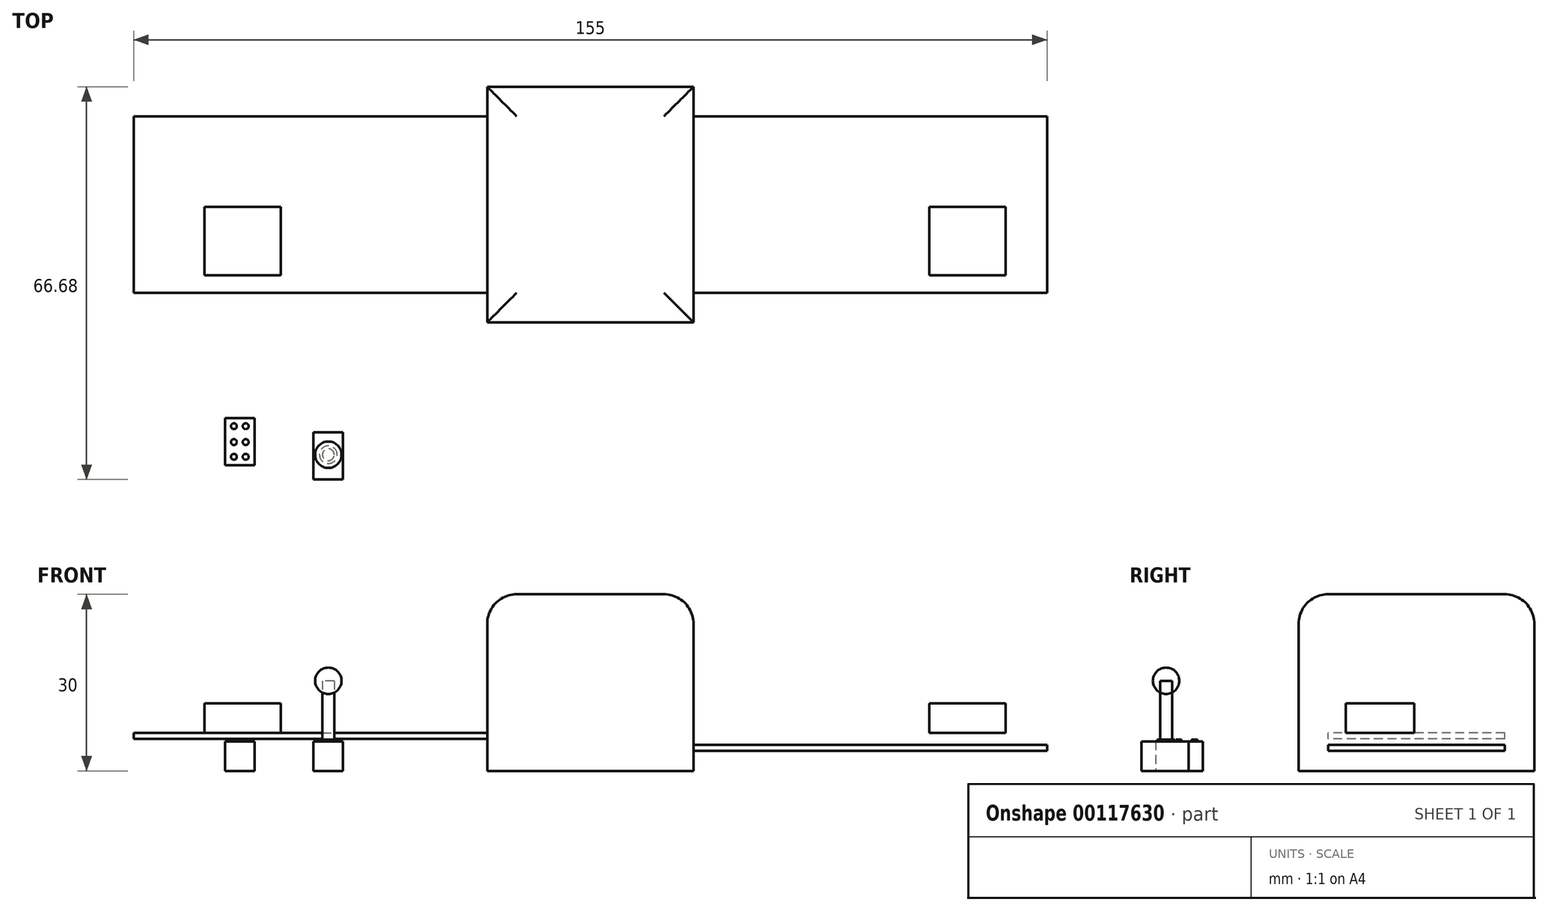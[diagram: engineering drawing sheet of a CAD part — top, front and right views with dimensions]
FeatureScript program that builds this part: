
annotation { "Feature Type Name" : "Feature", "Feature Type Description" : "" }
export const myFeature = defineFeature(function(context is Context, id is Id, definition is map)
    precondition{}
    {
        {
            var Q0;
            Q0=qCreatedBy(makeId("Top.planeOp"),FACE);
            var sketch = newSketch(context, id + "F0", { "sketchPlane" : qUnion([Q0])});
            skLineSegment(sketch, "E0.bottom", {"start": v(-16.65, 20.38) * mm, "end": v(18.35, 20.38) * mm});
            skLineSegment(sketch, "E0.top", {"start": v(-16.65, -19.62) * mm, "end": v(18.35, -19.62) * mm});
            skLineSegment(sketch, "E0.left", {"start": v(-16.65, 20.38) * mm, "end": v(-16.65, -19.62) * mm});
            skLineSegment(sketch, "E0.right", {"start": v(18.35, 20.38) * mm, "end": v(18.35, -19.62) * mm});
            skSolve(sketch);
        }
        {
            var Q0;
            Q0=makeQuery(id+"F0.imprint","IMPRINT",FACE,{"disambiguationData":[TD([[makeQuery(id+"F0.imprint","IMPRINT",EDGE,{"derivedFrom":sQuery(id+"F0.wireOp",EDGE,"E0.bottom")}),-1.0]])]});
            extrude(context, id + "F1", {"entities" : qUnion([Q0]), "depth" : 30 * mm});
        }
        {
            var Q0;
            Q0=makeQuery(id+"F1.opExtrude","CAP_EDGE",EDGE,{"disambiguationData":[OSD([sQuery(id+"F0.wireOp",EDGE,"E0.left")])],"isStart":false});
            var Q1;
            Q1=makeQuery(id+"F1.opExtrude","CAP_EDGE",EDGE,{"disambiguationData":[OSD([sQuery(id+"F0.wireOp",EDGE,"E0.right")])],"isStart":false});
            var Q2;
            Q2=makeQuery(id+"F1.opExtrude","CAP_EDGE",EDGE,{"disambiguationData":[OSD([sQuery(id+"F0.wireOp",EDGE,"E0.bottom")])],"isStart":false});
            var Q3;
            Q3=makeQuery(id+"F1.opExtrude","CAP_EDGE",EDGE,{"disambiguationData":[OSD([sQuery(id+"F0.wireOp",EDGE,"E0.top")])],"isStart":false});
            fillet(context, id + "F2", {"entities" : qUnion([Q0, Q1, Q2, Q3]), "radius" : 5 * mm, "tangentPropagation" : true, "allowEdgeOverflow" : false});
        }
        {
            var Q0;
            Q0=makeQuery(id+"F1.opExtrude","SWEPT_FACE",FACE,{"disambiguationData":[OSD([sQuery(id+"F0.wireOp",EDGE,"E0.right")])]});
            var sketch = newSketch(context, id + "F3", { "sketchPlane" : qUnion([Q0])});
            skLineSegment(sketch, "E1.bottom", {"start": v(15.38, 4.43) * mm, "end": v(-14.62, 4.43) * mm});
            skLineSegment(sketch, "E1.top", {"start": v(15.38, 3.43) * mm, "end": v(-14.62, 3.43) * mm});
            skLineSegment(sketch, "E1.left", {"start": v(15.38, 4.43) * mm, "end": v(15.38, 3.43) * mm});
            skLineSegment(sketch, "E1.right", {"start": v(-14.62, 4.43) * mm, "end": v(-14.62, 3.43) * mm});
            skSolve(sketch);
        }
        {
            var Q0;
            Q0=makeQuery(id+"F3.imprint","IMPRINT",FACE,{"disambiguationData":[TD([[makeQuery(id+"F3.imprint","IMPRINT",EDGE,{"derivedFrom":sQuery(id+"F3.wireOp",EDGE,"E1.bottom")}),1.0]])]});
            extrude(context, id + "F4", {"entities" : qUnion([Q0]), "operationType" : NewBodyOperationType.ADD, "depth" : 60 * mm});
        }
        {
            var Q0;
            Q0=makeQuery(id+"F1.opExtrude","SWEPT_FACE",FACE,{"disambiguationData":[OSD([sQuery(id+"F0.wireOp",EDGE,"E0.left")])]});
            var sketch = newSketch(context, id + "F5", { "sketchPlane" : qUnion([Q0])});
            skLineSegment(sketch, "E2.bottom", {"start": v(-15.38, 5.45) * mm, "end": v(14.62, 5.45) * mm});
            skLineSegment(sketch, "E2.top", {"start": v(-15.38, 6.45) * mm, "end": v(14.62, 6.45) * mm});
            skLineSegment(sketch, "E2.left", {"start": v(-15.38, 5.45) * mm, "end": v(-15.38, 6.45) * mm});
            skLineSegment(sketch, "E2.right", {"start": v(14.62, 5.45) * mm, "end": v(14.62, 6.45) * mm});
            skSolve(sketch);
        }
        {
            var Q0;
            Q0=makeQuery(id+"F5.imprint","IMPRINT",FACE,{"disambiguationData":[TD([[makeQuery(id+"F5.imprint","IMPRINT",EDGE,{"derivedFrom":sQuery(id+"F5.wireOp",EDGE,"E2.bottom")}),1.0]])]});
            extrude(context, id + "F6", {"entities" : qUnion([Q0]), "operationType" : NewBodyOperationType.ADD, "depth" : 60 * mm});
        }
        {
            var Q0;
            Q0=makeQuery(id+"F6.opExtrude","SWEPT_FACE",FACE,{"disambiguationData":[OSD([sQuery(id+"F5.wireOp",EDGE,"E2.top")])]});
            var sketch = newSketch(context, id + "F7", { "sketchPlane" : qUnion([Q0])});
            skLineSegment(sketch, "E3.bottom", {"start": v(-64.65, 0) * mm, "end": v(-51.65, 0) * mm});
            skLineSegment(sketch, "E3.top", {"start": v(-64.65, -11.62) * mm, "end": v(-51.65, -11.62) * mm});
            skLineSegment(sketch, "E3.left", {"start": v(-64.65, 0) * mm, "end": v(-64.65, -11.62) * mm});
            skLineSegment(sketch, "E3.right", {"start": v(-51.65, 0) * mm, "end": v(-51.65, -11.62) * mm});
            skLineSegment(sketch, "E4.bottom", {"start": v(58.35, 0) * mm, "end": v(71.35, 0) * mm});
            skLineSegment(sketch, "E4.top", {"start": v(58.35, -11.62) * mm, "end": v(71.35, -11.62) * mm});
            skLineSegment(sketch, "E4.left", {"start": v(58.35, 0) * mm, "end": v(58.35, -11.62) * mm});
            skLineSegment(sketch, "E4.right", {"start": v(71.35, 0) * mm, "end": v(71.35, -11.62) * mm});
            skSolve(sketch);
        }
        {
            var Q0;
            Q0=makeQuery(id+"F7.imprint","IMPRINT",FACE,{"disambiguationData":[TD([[makeQuery(id+"F7.imprint","IMPRINT",EDGE,{"derivedFrom":sQuery(id+"F7.wireOp",EDGE,"E3.bottom")}),-1.0]])]});
            var Q1;
            Q1=makeQuery(id+"F7.imprint","IMPRINT",FACE,{"disambiguationData":[TD([[makeQuery(id+"F7.imprint","IMPRINT",EDGE,{"derivedFrom":sQuery(id+"F7.wireOp",EDGE,"E4.bottom")}),-1.0]])]});
            extrude(context, id + "F8", {"entities" : qUnion([Q0, Q1]), "operationType" : NewBodyOperationType.ADD, "depth" : 5 * mm});
        }
        {
            var Q0;
            Q0=qCreatedBy(makeId("Top.planeOp"),FACE);
            var sketch = newSketch(context, id + "F9", { "sketchPlane" : qUnion([Q0])});
            skLineSegment(sketch, "E5.bottom", {"start": v(-61.14, -35.86) * mm, "end": v(-56.14, -35.86) * mm});
            skLineSegment(sketch, "E5.top", {"start": v(-61.14, -43.86) * mm, "end": v(-56.14, -43.86) * mm});
            skLineSegment(sketch, "E5.left", {"start": v(-61.14, -35.86) * mm, "end": v(-61.14, -43.86) * mm});
            skLineSegment(sketch, "E5.right", {"start": v(-56.14, -35.86) * mm, "end": v(-56.14, -43.86) * mm});
            skLineSegment(sketch, "E6.bottom", {"start": v(-46.14, -38.3) * mm, "end": v(-41.14, -38.3) * mm});
            skLineSegment(sketch, "E6.top", {"start": v(-46.14, -46.3) * mm, "end": v(-41.14, -46.3) * mm});
            skLineSegment(sketch, "E6.left", {"start": v(-46.14, -38.3) * mm, "end": v(-46.14, -46.3) * mm});
            skLineSegment(sketch, "E6.right", {"start": v(-41.14, -38.3) * mm, "end": v(-41.14, -46.3) * mm});
            skSolve(sketch);
        }
        {
            var Q0;
            Q0=makeQuery(id+"F9.imprint","IMPRINT",FACE,{"disambiguationData":[TD([[makeQuery(id+"F9.imprint","IMPRINT",EDGE,{"derivedFrom":sQuery(id+"F9.wireOp",EDGE,"E5.bottom")}),-1.0]])]});
            var Q1;
            Q1=makeQuery(id+"F9.imprint","IMPRINT",FACE,{"disambiguationData":[TD([[makeQuery(id+"F9.imprint","IMPRINT",EDGE,{"derivedFrom":sQuery(id+"F9.wireOp",EDGE,"E6.bottom")}),-1.0]])]});
            extrude(context, id + "F10", {"entities" : qUnion([Q0, Q1]), "depth" : 5 * mm});
        }
        {
            var Q0;
            Q0=makeQuery(id+"F10.opExtrude","CAP_FACE",FACE,{"disambiguationData":[OSD([sQuery(id+"F9.wireOp",EDGE,"E5.bottom"),sQuery(id+"F9.wireOp",EDGE,"E5.top"),sQuery(id+"F9.wireOp",EDGE,"E5.left"),sQuery(id+"F9.wireOp",EDGE,"E5.right")])],"isStart":false});
            var sketch = newSketch(context, id + "F11", { "sketchPlane" : qUnion([Q0])});
            skCircle(sketch, "E7", {"center": v(-59.64, -37.26) * mm, "radius": 0.5 * mm});
            skCircle(sketch, "E8", {"center": v(-57.64, -37.26) * mm, "radius": 0.5 * mm});
            skCircle(sketch, "E9", {"center": v(-59.64, -39.96) * mm, "radius": 0.5 * mm});
            skCircle(sketch, "E10", {"center": v(-57.64, -39.96) * mm, "radius": 0.5 * mm});
            skCircle(sketch, "E11", {"center": v(-59.64, -42.46) * mm, "radius": 0.5 * mm});
            skCircle(sketch, "E12", {"center": v(-57.64, -42.46) * mm, "radius": 0.5 * mm});
            skSolve(sketch);
        }
        {
            var Q0;
            Q0=makeQuery(id+"F11.imprint","IMPRINT",FACE,{"disambiguationData":[TD([[makeQuery(id+"F11.imprint","IMPRINT",EDGE,{"derivedFrom":sQuery(id+"F11.wireOp",EDGE,"E7")}),1.0]])]});
            var Q1;
            Q1=makeQuery(id+"F11.imprint","IMPRINT",FACE,{"disambiguationData":[TD([[makeQuery(id+"F11.imprint","IMPRINT",EDGE,{"derivedFrom":sQuery(id+"F11.wireOp",EDGE,"E8")}),1.0]])]});
            var Q2;
            Q2=makeQuery(id+"F11.imprint","IMPRINT",FACE,{"disambiguationData":[TD([[makeQuery(id+"F11.imprint","IMPRINT",EDGE,{"derivedFrom":sQuery(id+"F11.wireOp",EDGE,"E9")}),1.0]])]});
            var Q3;
            Q3=makeQuery(id+"F11.imprint","IMPRINT",FACE,{"disambiguationData":[TD([[makeQuery(id+"F11.imprint","IMPRINT",EDGE,{"derivedFrom":sQuery(id+"F11.wireOp",EDGE,"E10")}),1.0]])]});
            var Q4;
            Q4=makeQuery(id+"F11.imprint","IMPRINT",FACE,{"disambiguationData":[TD([[makeQuery(id+"F11.imprint","IMPRINT",EDGE,{"derivedFrom":sQuery(id+"F11.wireOp",EDGE,"E11")}),1.0]])]});
            var Q5;
            Q5=makeQuery(id+"F11.imprint","IMPRINT",FACE,{"disambiguationData":[TD([[makeQuery(id+"F11.imprint","IMPRINT",EDGE,{"derivedFrom":sQuery(id+"F11.wireOp",EDGE,"E12")}),1.0]])]});
            extrude(context, id + "F12", {"entities" : qUnion([Q0, Q1, Q2, Q3, Q4, Q5]), "operationType" : NewBodyOperationType.ADD, "depth" : 0.3 * mm});
        }
        {
            var Q0;
            Q0=makeQuery(id+"F10.opExtrude","CAP_FACE",FACE,{"disambiguationData":[OSD([sQuery(id+"F9.wireOp",EDGE,"E6.bottom"),sQuery(id+"F9.wireOp",EDGE,"E6.top"),sQuery(id+"F9.wireOp",EDGE,"E6.left"),sQuery(id+"F9.wireOp",EDGE,"E6.right")])],"isStart":false});
            var sketch = newSketch(context, id + "F13", { "sketchPlane" : qUnion([Q0])});
            skCircle(sketch, "E13", {"center": v(-43.61, -42.1) * mm, "radius": 1.5 * mm});
            skSolve(sketch);
        }
        {
            var Q0;
            Q0=makeQuery(id+"F13.imprint","IMPRINT",FACE,{"disambiguationData":[TD([[makeQuery(id+"F13.imprint","IMPRINT",EDGE,{"derivedFrom":sQuery(id+"F13.wireOp",EDGE,"E13")}),1.0]])]});
            extrude(context, id + "F14", {"entities" : qUnion([Q0]), "operationType" : NewBodyOperationType.ADD, "depth" : 0.3 * mm});
        }
        {
            var Q0;
            Q0=makeQuery(id+"F14.opExtrude","CAP_FACE",FACE,{"disambiguationData":[OSD([sQuery(id+"F13.wireOp",EDGE,"E13")])],"isStart":false});
            var sketch = newSketch(context, id + "F15", { "sketchPlane" : qUnion([Q0])});
            skCircle(sketch, "E14", {"center": v(-43.61, -42.1) * mm, "radius": 1 * mm});
            skSolve(sketch);
        }
        {
            var Q0;
            Q0=makeQuery(id+"F15.imprint","IMPRINT",FACE,{"disambiguationData":[TD([[makeQuery(id+"F15.imprint","IMPRINT",EDGE,{"derivedFrom":sQuery(id+"F15.wireOp",EDGE,"E14")}),1.0]])]});
            extrude(context, id + "F16", {"entities" : qUnion([Q0]), "operationType" : NewBodyOperationType.ADD, "depth" : 10 * mm});
        }
        {
            var Q0;
            Q0=makeQuery(id+"F16.opExtrude","CAP_FACE",FACE,{"disambiguationData":[OSD([sQuery(id+"F15.wireOp",EDGE,"E14")])],"isStart":false});
            var sketch = newSketch(context, id + "F17", { "sketchPlane" : qUnion([Q0])});
            skArc(sketch, "E15", {"start": v(-43.61, -44.34) * mm, "mid": v(-41.37, -42.1) * mm, "end": v(-43.61, -39.86) * mm});
            skLineSegment(sketch, "E16", {"start": v(-43.61, -42.1) * mm, "end": v(-43.61, -39.86) * mm});
            skLineSegment(sketch, "E17", {"start": v(-43.61, -42.1) * mm, "end": v(-43.61, -44.34) * mm});
            skSolve(sketch);
        }
        {
            var Q0;
            Q0 = qSketchRegion(id + "F17", true);
            var Q1;
            Q1=sQuery(id+"F17.wireOp",EDGE,"E16");
            revolve(context, id + "F18", {"entities" : qUnion([Q0]), "axis" : qUnion([Q1]), "revolveType" : RevolveType.FULL});
        }
    });
